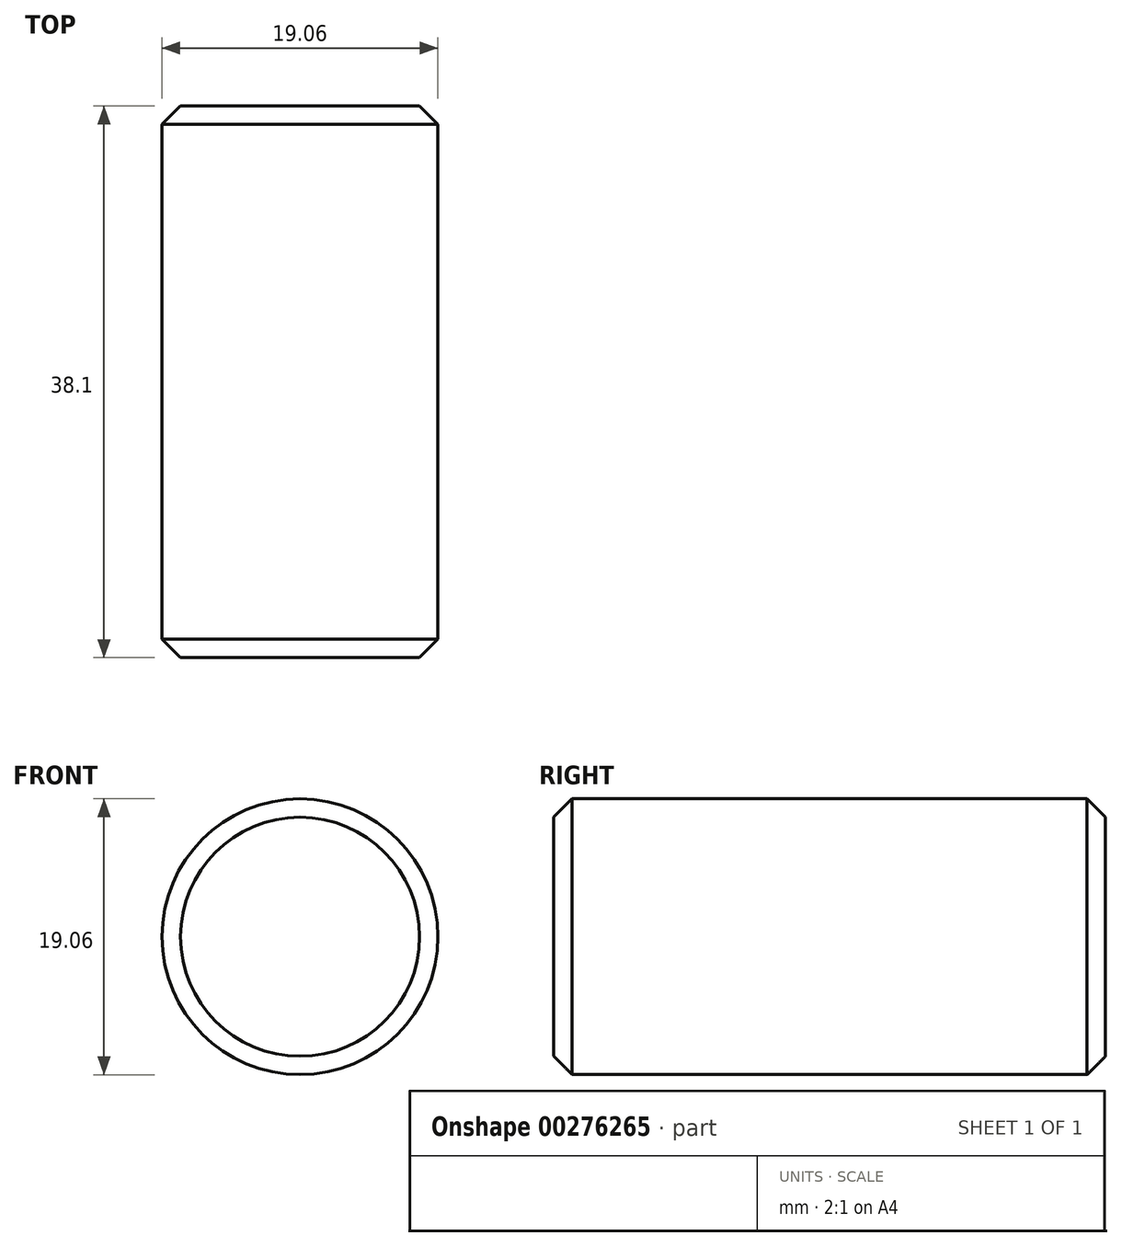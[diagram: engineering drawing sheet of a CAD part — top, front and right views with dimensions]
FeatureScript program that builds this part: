
annotation { "Feature Type Name" : "Feature", "Feature Type Description" : "" }
export const myFeature = defineFeature(function(context is Context, id is Id, definition is map)
    precondition{}
    {
        {
            var Q0;
            Q0=qCreatedBy(makeId("Front.planeOp"),FACE);
            var sketch = newSketch(context, id + "F0", { "sketchPlane" : qUnion([Q0])});
            skCircle(sketch, "E0", {"center": v(0, 0) * mm, "radius": 9.53 * mm});
            skSolve(sketch);
        }
        {
            var Q0;
            Q0 = qSketchRegion(id + "F0", true);
            extrude(context, id + "F1", {"entities" : qUnion([Q0]), "depth" : 38.1 * mm});
        }
        {
            var Q0;
            Q0=makeQuery(id+"F1.opExtrude","CAP_EDGE",EDGE,{"disambiguationData":[OSD([sQuery(id+"F0.wireOp",EDGE,"E0")])],"isStart":false});
            var Q1;
            Q1=makeQuery(id+"F1.opExtrude","CAP_EDGE",EDGE,{"disambiguationData":[OSD([sQuery(id+"F0.wireOp",EDGE,"E0")])],"isStart":true});
            chamfer(context, id + "F2", {"entities" : qUnion([Q0, Q1]), "chamferType" : ChamferType.OFFSET_ANGLE, "width" : 1.27 * mm, "oppositeDirection" : false, "angle" : 45 * degree, "tangentPropagation" : true});
        }
    });
